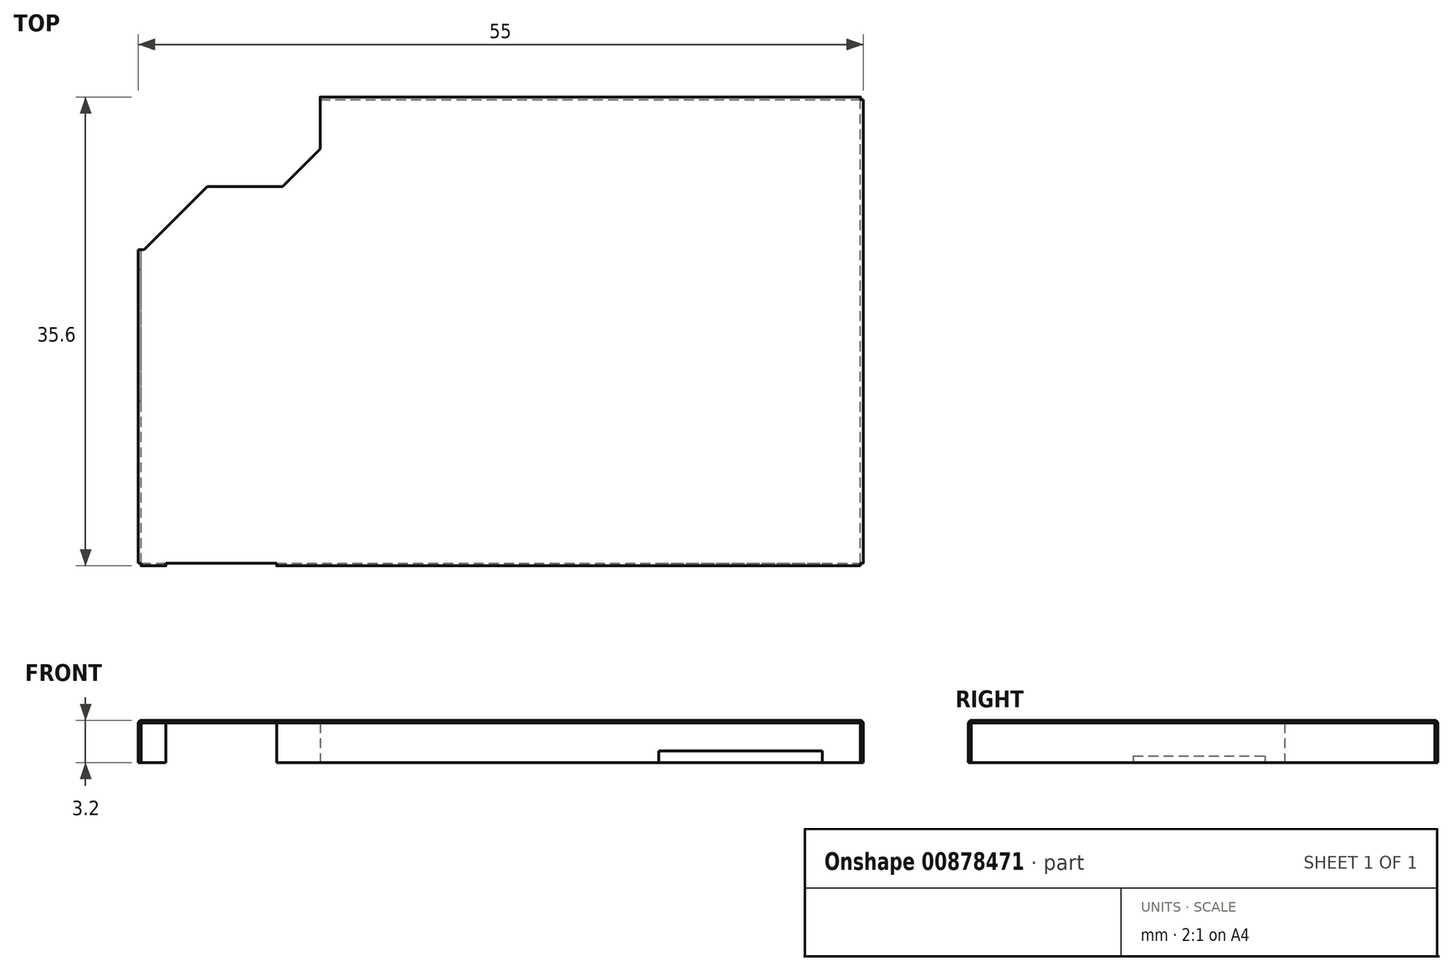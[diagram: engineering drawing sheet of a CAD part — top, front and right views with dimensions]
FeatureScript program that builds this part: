
annotation { "Feature Type Name" : "Feature", "Feature Type Description" : "" }
export const myFeature = defineFeature(function(context is Context, id is Id, definition is map)
    precondition{}
    {
        {
            var Q0;
            Q0=qCreatedBy(makeId("Top.planeOp"),FACE);
            var sketch = newSketch(context, id + "F0", { "sketchPlane" : qUnion([Q0])});
            skLineSegment(sketch, "E0", {"start": v(-26.8, -17.6) * mm, "end": v(-26.8, 6.2) * mm});
            skLineSegment(sketch, "E1", {"start": v(28.2, -17.6) * mm, "end": v(28.2, 17.6) * mm});
            skLineSegment(sketch, "E2", {"start": v(-26.6, -17.8) * mm, "end": v(28, -17.8) * mm});
            skLineSegment(sketch, "E3", {"start": v(-26.8, -17.6) * mm, "end": v(-26.6, -17.6) * mm});
            skLineSegment(sketch, "E4", {"start": v(-26.6, -17.6) * mm, "end": v(-26.6, -17.8) * mm});
            skLineSegment(sketch, "E5", {"start": v(28, -17.8) * mm, "end": v(28, -17.6) * mm});
            skLineSegment(sketch, "E6", {"start": v(28, -17.6) * mm, "end": v(28.2, -17.6) * mm});
            skLineSegment(sketch, "E7", {"start": v(-13, 17.6) * mm, "end": v(28, 17.6) * mm});
            skLineSegment(sketch, "E8", {"start": v(-13, 17.8) * mm, "end": v(28, 17.8) * mm});
            skLineSegment(sketch, "E9", {"start": v(-26.6, -17.6) * mm, "end": v(-26.6, 6.2) * mm});
            skLineSegment(sketch, "E10", {"start": v(-26.6, -17.6) * mm, "end": v(28, -17.6) * mm});
            skLineSegment(sketch, "E11", {"start": v(28, -17.6) * mm, "end": v(28, 17.6) * mm});
            skLineSegment(sketch, "E12", {"start": v(28, 17.8) * mm, "end": v(28, 17.6) * mm});
            skLineSegment(sketch, "E13", {"start": v(28, 17.6) * mm, "end": v(28.2, 17.6) * mm});
            skLineSegment(sketch, "E14", {"start": v(-13, 17.8) * mm, "end": v(-13, 13.84) * mm});
            skLineSegment(sketch, "E15", {"start": v(-26.38, 6.2) * mm, "end": v(-26.8, 6.2) * mm});
            skLineSegment(sketch, "E16", {"start": v(-24.7, -17.6) * mm, "end": v(-24.7, -17.8) * mm});
            skLineSegment(sketch, "E17", {"start": v(-16.3, -17.6) * mm, "end": v(-16.3, -17.8) * mm});
            skLineSegment(sketch, "E18", {"start": v(12.7, -17.6) * mm, "end": v(12.7, -17.8) * mm});
            skLineSegment(sketch, "E19", {"start": v(25.1, -17.6) * mm, "end": v(25.1, -17.8) * mm});
            skLineSegment(sketch, "E20", {"start": v(-13, 13.84) * mm, "end": v(-15.84, 11) * mm});
            skLineSegment(sketch, "E21", {"start": v(-15.84, 11) * mm, "end": v(-21.58, 11) * mm});
            skLineSegment(sketch, "E22", {"start": v(-21.58, 11) * mm, "end": v(-26.38, 6.2) * mm});
            skLineSegment(sketch, "E23", {"start": v(-26.8, 4.7) * mm, "end": v(-26.6, 4.7) * mm});
            skLineSegment(sketch, "E24", {"start": v(-26.8, -5.3) * mm, "end": v(-26.6, -5.3) * mm});
            skSolve(sketch);
        }
        {
            var Q0;
            {var subQ0=sQuery(id+"F0.wireOp",EDGE,"E3");Q0=makeQuery(id+"F0.imprint","IMPRINT",FACE,{"disambiguationData":[TD([[makeQuery(id+"F0.imprint","IMPRINT",EDGE,{"derivedFrom":subQ0}),1.0]])]});}
            var Q1;
            {var subQ0=sQuery(id+"F0.wireOp",EDGE,"E4");Q1=makeQuery(id+"F0.imprint","IMPRINT",FACE,{"disambiguationData":[TD([[makeQuery(id+"F0.imprint","IMPRINT",EDGE,{"derivedFrom":subQ0}),1.0]])]});}
            var Q2;
            {var subQ0=sQuery(id+"F0.wireOp",EDGE,"E17");Q2=makeQuery(id+"F0.imprint","IMPRINT",FACE,{"disambiguationData":[TD([[makeQuery(id+"F0.imprint","IMPRINT",EDGE,{"derivedFrom":subQ0}),1.0]])]});}
            var Q3;
            {var subQ0=sQuery(id+"F0.wireOp",EDGE,"E23");Q3=makeQuery(id+"F0.imprint","IMPRINT",FACE,{"disambiguationData":[TD([[makeQuery(id+"F0.imprint","IMPRINT",EDGE,{"derivedFrom":subQ0}),-1.0]])]});}
            var Q4;
            {var subQ3=sQuery(id+"F0.wireOp",EDGE,"E23");Q4=makeQuery(id+"F0.imprint","IMPRINT",FACE,{"disambiguationData":[TD([[makeQuery(id+"F0.imprint","IMPRINT",EDGE,{"derivedFrom":subQ3}),1.0]])]});}
            var Q5;
            {var subQ0=sQuery(id+"F0.wireOp",EDGE,"E7");Q5=makeQuery(id+"F0.imprint","IMPRINT",FACE,{"disambiguationData":[TD([[makeQuery(id+"F0.imprint","IMPRINT",EDGE,{"derivedFrom":subQ0}),1.0]])]});}
            var Q6;
            Q6=makeQuery(id+"F0.imprint","IMPRINT",FACE,{"disambiguationData":[TD([[makeQuery(id+"F0.imprint","IMPRINT",EDGE,{"derivedFrom":sQuery(id+"F0.wireOp",EDGE,"E1")}),1.0]])]});
            var Q7;
            {var subQ0=sQuery(id+"F0.wireOp",EDGE,"E5");Q7=makeQuery(id+"F0.imprint","IMPRINT",FACE,{"disambiguationData":[TD([[makeQuery(id+"F0.imprint","IMPRINT",EDGE,{"derivedFrom":subQ0}),1.0]])]});}
            var Q8;
            {var subQ0=sQuery(id+"F0.wireOp",EDGE,"E18");Q8=makeQuery(id+"F0.imprint","IMPRINT",FACE,{"disambiguationData":[TD([[makeQuery(id+"F0.imprint","IMPRINT",EDGE,{"derivedFrom":subQ0}),1.0]])]});}
            extrude(context, id + "F1", {"entities" : qUnion([Q0, Q1, Q2, Q3, Q4, Q5, Q6, Q7, Q8]), "depth" : 3 * mm, "offsetDistance" : 25 * mm});
        }
        {
            var Q0;
            {var subQ0=sQuery(id+"F0.wireOp",EDGE,"E3");Q0=makeQuery(id+"F0.imprint","IMPRINT",FACE,{"disambiguationData":[TD([[makeQuery(id+"F0.imprint","IMPRINT",EDGE,{"derivedFrom":subQ0}),1.0]])]});}
            var Q1;
            {var subQ8=sQuery(id+"F0.wireOp",EDGE,"E7");Q1=makeQuery(id+"F0.imprint","IMPRINT",FACE,{"disambiguationData":[TD([[makeQuery(id+"F0.imprint","IMPRINT",EDGE,{"derivedFrom":subQ8}),-1.0]])]});}
            var Q2;
            {var subQ0=sQuery(id+"F0.wireOp",EDGE,"E4");Q2=makeQuery(id+"F0.imprint","IMPRINT",FACE,{"disambiguationData":[TD([[makeQuery(id+"F0.imprint","IMPRINT",EDGE,{"derivedFrom":subQ0}),1.0]])]});}
            var Q3;
            {var subQ0=sQuery(id+"F0.wireOp",EDGE,"E17");Q3=makeQuery(id+"F0.imprint","IMPRINT",FACE,{"disambiguationData":[TD([[makeQuery(id+"F0.imprint","IMPRINT",EDGE,{"derivedFrom":subQ0}),1.0]])]});}
            var Q4;
            {var subQ0=sQuery(id+"F0.wireOp",EDGE,"E18");Q4=makeQuery(id+"F0.imprint","IMPRINT",FACE,{"disambiguationData":[TD([[makeQuery(id+"F0.imprint","IMPRINT",EDGE,{"derivedFrom":subQ0}),1.0]])]});}
            var Q5;
            {var subQ0=sQuery(id+"F0.wireOp",EDGE,"E5");Q5=makeQuery(id+"F0.imprint","IMPRINT",FACE,{"disambiguationData":[TD([[makeQuery(id+"F0.imprint","IMPRINT",EDGE,{"derivedFrom":subQ0}),1.0]])]});}
            var Q6;
            Q6=makeQuery(id+"F0.imprint","IMPRINT",FACE,{"disambiguationData":[TD([[makeQuery(id+"F0.imprint","IMPRINT",EDGE,{"derivedFrom":sQuery(id+"F0.wireOp",EDGE,"E1")}),1.0]])]});
            var Q7;
            {var subQ0=sQuery(id+"F0.wireOp",EDGE,"E7");Q7=makeQuery(id+"F0.imprint","IMPRINT",FACE,{"disambiguationData":[TD([[makeQuery(id+"F0.imprint","IMPRINT",EDGE,{"derivedFrom":subQ0}),1.0]])]});}
            var Q8;
            {var subQ3=sQuery(id+"F0.wireOp",EDGE,"E23");Q8=makeQuery(id+"F0.imprint","IMPRINT",FACE,{"disambiguationData":[TD([[makeQuery(id+"F0.imprint","IMPRINT",EDGE,{"derivedFrom":subQ3}),1.0]])]});}
            var Q9;
            {var subQ0=sQuery(id+"F0.wireOp",EDGE,"E23");Q9=makeQuery(id+"F0.imprint","IMPRINT",FACE,{"disambiguationData":[TD([[makeQuery(id+"F0.imprint","IMPRINT",EDGE,{"derivedFrom":subQ0}),-1.0]])]});}
            extrude(context, id + "F2", {"entities" : qUnion([Q0, Q1, Q2, Q3, Q4, Q5, Q6, Q7, Q8, Q9]), "depth" : 3.2 * mm, "offsetDistance" : 25 * mm, "hasSecondDirection" : true, "secondDirectionOppositeDirection" : false, "secondDirectionDepth" : 3 * mm});
        }
        {
            var Q0;
            {var subQ0=sQuery(id+"F0.wireOp",EDGE,"E18");Q0=makeQuery(id+"F0.imprint","IMPRINT",FACE,{"disambiguationData":[TD([[makeQuery(id+"F0.imprint","IMPRINT",EDGE,{"derivedFrom":subQ0}),1.0]])]});}
            extrude(context, id + "F3", {"entities" : qUnion([Q0]), "operationType" : NewBodyOperationType.REMOVE, "depth" : 0.9 * mm, "offsetDistance" : 25 * mm});
        }
        {
            var Q0;
            {var subQ0=sQuery(id+"F0.wireOp",EDGE,"E23");Q0=makeQuery(id+"F0.imprint","IMPRINT",FACE,{"disambiguationData":[TD([[makeQuery(id+"F0.imprint","IMPRINT",EDGE,{"derivedFrom":subQ0}),-1.0]])]});}
            extrude(context, id + "F4", {"entities" : qUnion([Q0]), "operationType" : NewBodyOperationType.REMOVE, "depth" : 0.5 * mm, "offsetDistance" : 25 * mm});
        }
        {
            var Q0;
            Q0=makeQuery(id+"F2.opExtrude","CAP_EDGE",EDGE,{"disambiguationData":[OSD([sQuery(id+"F0.wireOp",EDGE,"E2")])],"isStart":false});
            var Q1;
            Q1=makeQuery(id+"F2.opExtrude","CAP_EDGE",EDGE,{"disambiguationData":[OSD([sQuery(id+"F0.wireOp",EDGE,"E0")])],"isStart":false});
            var Q2;
            Q2=makeQuery(id+"F2.opExtrude","CAP_EDGE",EDGE,{"disambiguationData":[OSD([sQuery(id+"F0.wireOp",EDGE,"E8")])],"isStart":false});
            var Q3;
            Q3=makeQuery(id+"F2.opExtrude","CAP_EDGE",EDGE,{"disambiguationData":[OSD([sQuery(id+"F0.wireOp",EDGE,"E1")])],"isStart":false});
            fillet(context, id + "F5", {"entities" : qUnion([Q0, Q1, Q2, Q3]), "radius" : 0.2 * mm, "tangentPropagation" : true, "allowEdgeOverflow" : false});
        }
    });
